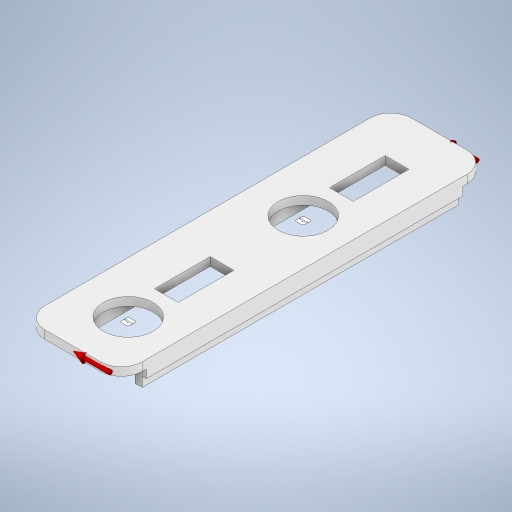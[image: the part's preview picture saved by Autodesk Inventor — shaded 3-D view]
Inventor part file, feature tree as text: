
AUTODESK INVENTOR PART (.ipt)
format: ipt  version: 2024.1 (Build 281209000, 209)  size: 373,760 bytes
history: native  units: mm
features: extrude x3, sketch x2, other x1
ambient origin geometry x8: Origin, YZ Plane, XZ Plane, XY Plane, X Axis, Y Axis, Z Axis, Center Point
bodies: Body1 (feature_tree)
feature tree (6):
  other  "Sólido1"
  extrude  "Extrusión1"  Depth=132.0mm
  sketch  "Boceto2"  dims[d2=7.5mm d5=8.5mm d8=20.0mm d9=12.0mm d10=43.0mm d11=16.5mm d12=13.5mm d13=16.5mm d15=18.0mm d16=13.5mm d17=3.0mm d18=0.0mm d19=4.0mm d20=114.0mm d21=2.5mm d22=2.5mm d23=24.0mm d24=6.5mm d25=0.0mm d26=3.0mm d27=0.0mm d28=0.5mm d29=0.872665mm]
  extrude  "Extrusión2"  Depth=8.5mm
  extrude  "Extrusión3"  Depth=20.0mm
  sketch  "Boceto1"  dims[d0=35.0mm d1=132.0mm]
